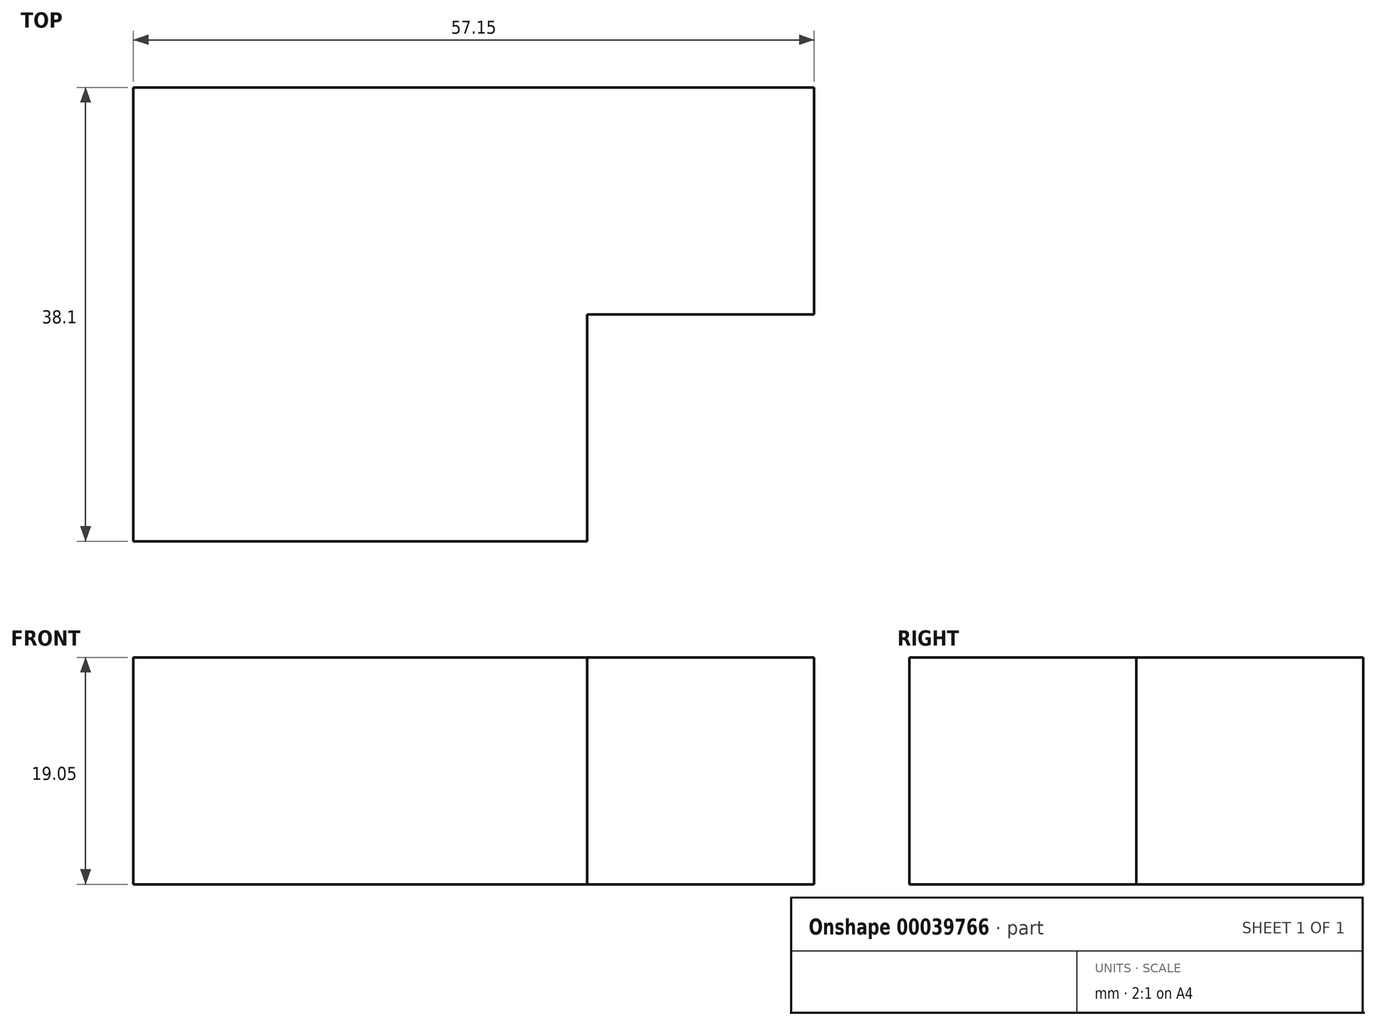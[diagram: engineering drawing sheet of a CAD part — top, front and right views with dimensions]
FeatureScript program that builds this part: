
annotation { "Feature Type Name" : "Feature", "Feature Type Description" : "" }
export const myFeature = defineFeature(function(context is Context, id is Id, definition is map)
    precondition{}
    {
        {
            var Q0;
            Q0=qCreatedBy(makeId("Top.planeOp"),FACE);
            var sketch = newSketch(context, id + "F0", { "sketchPlane" : qUnion([Q0])});
            skLineSegment(sketch, "E0.bottom", {"start": v(0, 0) * mm, "end": v(38.1, 0) * mm});
            skLineSegment(sketch, "E0.top", {"start": v(0, -38.1) * mm, "end": v(38.1, -38.1) * mm});
            skLineSegment(sketch, "E0.left", {"start": v(0, 0) * mm, "end": v(0, -38.1) * mm});
            skLineSegment(sketch, "E0.right", {"start": v(38.1, 0) * mm, "end": v(38.1, -38.1) * mm});
            skSolve(sketch);
        }
        {
            var Q0;
            Q0=makeQuery(id+"F0.imprint","IMPRINT",FACE,{"disambiguationData":[TD([[makeQuery(id+"F0.imprint","IMPRINT",EDGE,{"derivedFrom":sQuery(id+"F0.wireOp",EDGE,"E0.bottom")}),-1.0]])]});
            extrude(context, id + "F1", {"entities" : qUnion([Q0]), "depth" : 19.05 * mm});
        }
        {
            var Q0;
            Q0=makeQuery(id+"F1.opExtrude","SWEPT_FACE",FACE,{"disambiguationData":[OSD([sQuery(id+"F0.wireOp",EDGE,"E0.right")])]});
            var sketch = newSketch(context, id + "F2", { "sketchPlane" : qUnion([Q0])});
            skLineSegment(sketch, "E1.bottom", {"start": v(0, 0) * mm, "end": v(-19.05, 0) * mm});
            skLineSegment(sketch, "E1.top", {"start": v(0, 19.05) * mm, "end": v(-19.05, 19.05) * mm});
            skLineSegment(sketch, "E1.left", {"start": v(0, 0) * mm, "end": v(0, 19.05) * mm});
            skLineSegment(sketch, "E1.right", {"start": v(-19.05, 0) * mm, "end": v(-19.05, 19.05) * mm});
            skSolve(sketch);
        }
        {
            var Q0;
            Q0=makeQuery(id+"F2.imprint","IMPRINT",FACE,{"disambiguationData":[TD([[makeQuery(id+"F2.imprint","IMPRINT",EDGE,{"derivedFrom":sQuery(id+"F2.wireOp",EDGE,"E1.bottom")}),-1.0]])]});
            extrude(context, id + "F3", {"entities" : qUnion([Q0]), "operationType" : NewBodyOperationType.ADD, "depth" : 19.05 * mm});
        }
    });
